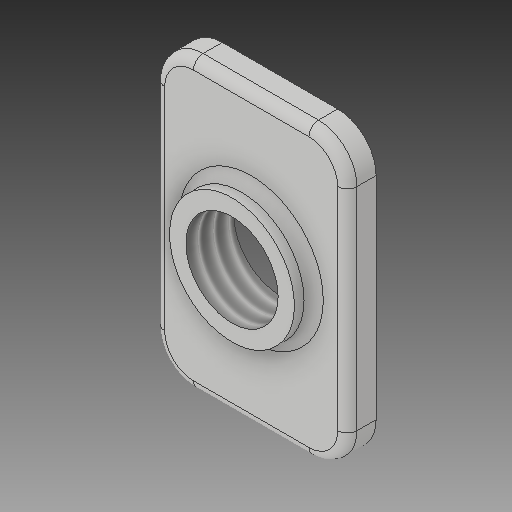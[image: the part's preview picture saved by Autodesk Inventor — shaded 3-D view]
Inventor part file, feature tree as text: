
AUTODESK INVENTOR PART (.ipt)
format: ipt  version: 2017 (Build 210142000, 142)  size: 163,328 bytes
history: native  units: mm
features: other x3, sketch x2
ambient origin geometry x8: Origin, YZ Plane, XZ Plane, XY Plane, X Axis, Y Axis, Z Axis, Center Point
bodies: Solid1 (feature_tree)
feature tree (5):
  other  "M5 Tee Nut_MIR_MIR_MIR.ipt"
  other  "Solid1::M5 Tee Nut_MIR_MIR_MIR.ipt"
  other  "TaggingFeature1"
  sketch  "Sketch1"  dims[d0=10.0mm]
  sketch  "Sketch2"
